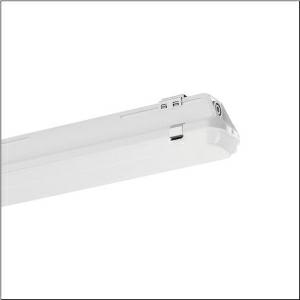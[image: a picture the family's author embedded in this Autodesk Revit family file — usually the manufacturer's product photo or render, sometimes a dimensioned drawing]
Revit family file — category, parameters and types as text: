
# Revit family: monsun_r__11_51fp12mp4b0u_05f5
name_source: partatom
category: Lighting Fixtures
units: mm (PartAtom-declared; Revit-internal decimal feet)

## family parameters
Cut with Voids When Loaded = No
Host = Face
Light Source = No
Part Type = Normal
Room Calculation Point = No
Round Connector Dimension = Use Diameter
Shared = No

## types (1)
- --- (1 x LED, 11850 lm, 62.4 W, 4000K)
    Apparent Load = 62 VA
    CIE Flux Codes = 62 86 96 97 100
    Color Rendering = 80
    Color Temperature = 4000K
    Default Elevation = 1800 mm
    Description = Monsun® 11, damp-proof luminaire, chain hanger, primary light control with lens, primary optical cover: enclosure, of PMMA, light emission: direct distribution, primary light characteristic: symmetric, installation type: suspended mounting, surface-mounted, horizontal mounting, vertical mounting, LED, rated luminous flux: 11.850lm, luminous efficacy: 190lm/W, light colour: 840, colour temperature: 4000K, control gear: ON/OFF Multilumen, with terminal, 3-pole, max. 2.5mm², mains connection: 220..240V, AC, 50/60Hz, rated input power: 62W, luminaire housing, of glass-fibre reinforced polyester, uncoated, bright grey, incl. chain hanger, length: 1.590mm, width: 90mm, height: 88mm, clip for enclosure, of stainless steel (V2A), ceiling mounting element, of stainless steel (V2A), chain hanger, of stainless steel (V2A), protection rating (complete): IP66, insulation class (complete): insulation class I (protective earthing), certification: CE, ENEC, VDE, UKCA, protection symbol: D, impact resistance: IK04, permissible operating ambient temperature: -35..+35°C, standard: EN 50419, EN 60598-2-1, contact your sales advisor before using the luminaires in applications with unclear chemical exposure, large temperature fluctuations or condensation-forming humidity, LABS conformity tested according to VDMA 24364:2018-05, no direct snow, no direct sun, no direct rain, for indoor or canopied outdoor use, corresponds to IFS (International Featured Standards) requirements for safety and quality in the food industry, packaging unit: 1 piece
    Height = 89 mm
    Lamp = 1 x LED
    Lamp Light Flux = 11850 lm
    Lamp Power = 62.4 W
    Lamp count = 1
    Length = 1590 mm
    Luminous efficacy = 190 lm/W
    Manufacturer = Siteco
    ModVariant = No
    Model = 51FP12MP4B0U
    Mounting Place = Ceiling
    Mounting Type = Surface mounted
    Number of Poles = 1
    OnlyDefault = Yes
    Power Factor = 1
    Product Name = Monsun® 11
    Product group = damp-proof luminaire
    ProductGroupID = 301
    Protection Class = Protection class I
    Protection Degree = IP 66
    RLX_Detail_Level = 1
    RLX_Emergency_Light_Flux = 0 lm
    RLX_Emergency_Type = 0
    RLX_Emergency_Type_DB = No
    RlxData = <blob elided: 90029 chars, md5=50e1482b>
    Socket = socket
    Standby Power = 0 W
    System Light Flux = 11850 lm
    System Power = 62 W
    Type Comments = factory setting: luminous flux: 100 % | (A | C | E) | 147 mA
    Type Image = l_1349237.jpg
    URL = http://relux.com
    VarID = @adj_038659
    Voltage = 0 V
    Weight = 0.00 kg
    Width = 90 mm

## geometry (parser evidence)
native form markers: Blend x4, Sweep x10
no freeform markers — native parametric forms only
